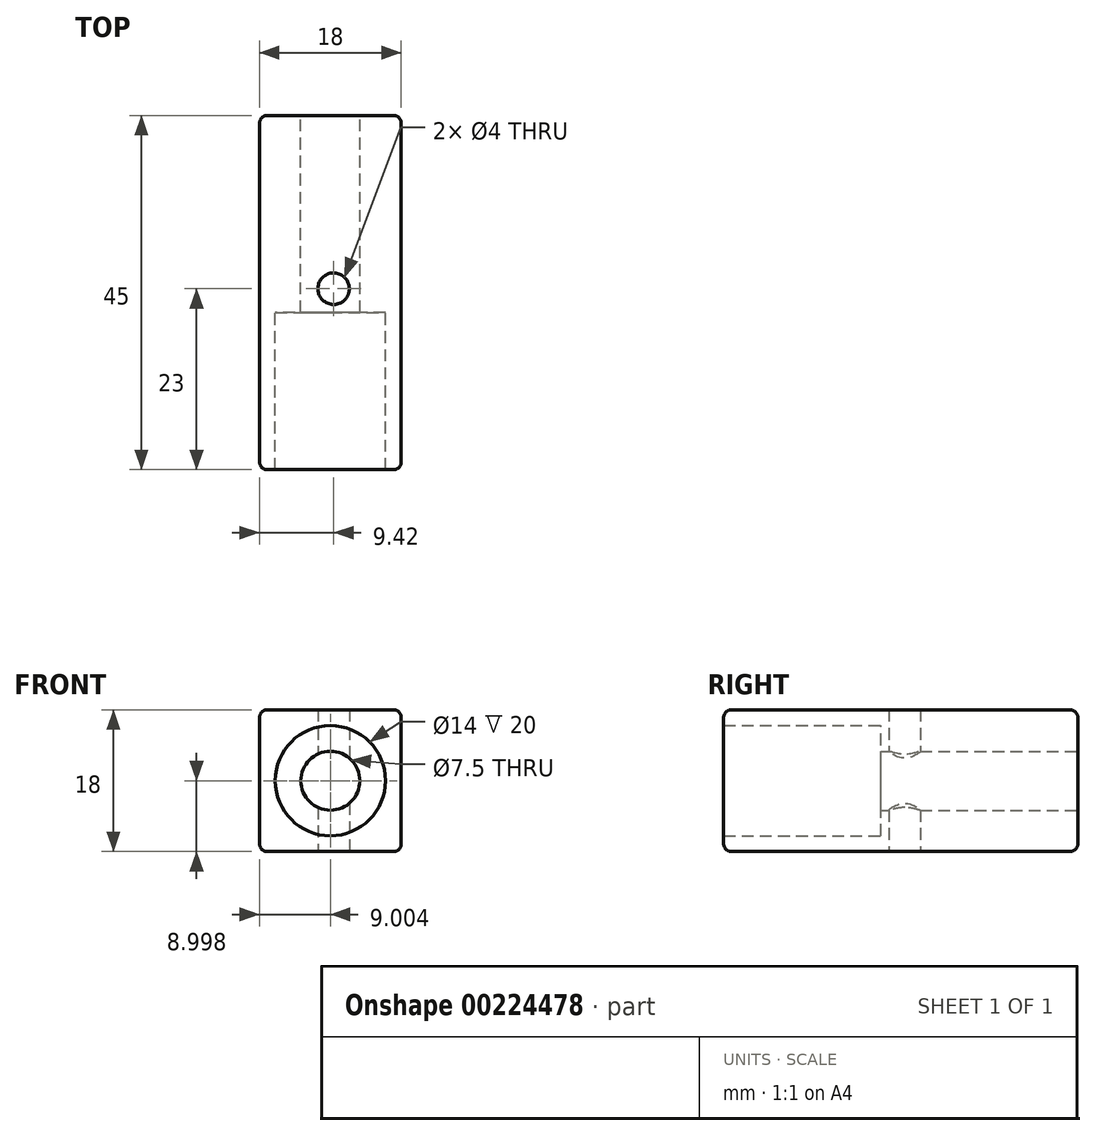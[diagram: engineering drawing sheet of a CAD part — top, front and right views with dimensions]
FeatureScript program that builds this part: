
annotation { "Feature Type Name" : "Feature", "Feature Type Description" : "" }
export const myFeature = defineFeature(function(context is Context, id is Id, definition is map)
    precondition{}
    {
        {
            var Q0;
            Q0=qCreatedBy(makeId("Front.planeOp"),FACE);
            var sketch = newSketch(context, id + "F0", { "sketchPlane" : qUnion([Q0])});
            skLineSegment(sketch, "E0.bottom", {"start": v(-9.42, 10.89) * mm, "end": v(8.58, 10.89) * mm});
            skLineSegment(sketch, "E0.top", {"start": v(-9.42, -7.11) * mm, "end": v(8.58, -7.11) * mm});
            skLineSegment(sketch, "E0.left", {"start": v(-9.42, 10.89) * mm, "end": v(-9.42, -7.11) * mm});
            skLineSegment(sketch, "E0.right", {"start": v(8.58, 10.89) * mm, "end": v(8.58, -7.11) * mm});
            skCircle(sketch, "E1", {"center": v(-0.42, 1.89) * mm, "radius": 7 * mm});
            skPoint(sketch, "E1.centerSnap0", {"position": v(-0.42, 10.89) * mm});
            skPoint(sketch, "E1.centerSnap1", {"position": v(8.58, 1.89) * mm});
            skCircle(sketch, "E2", {"center": v(-0.42, 1.89) * mm, "radius": 3.75 * mm});
            skSolve(sketch);
        }
        {
            var Q0;
            Q0=makeQuery(id+"F0.imprint","IMPRINT",FACE,{"disambiguationData":[TD([[makeQuery(id+"F0.imprint","IMPRINT",EDGE,{"derivedFrom":sQuery(id+"F0.wireOp",EDGE,"E0.bottom")}),-1.0]])]});
            extrude(context, id + "F1", {"entities" : qUnion([Q0]), "depth" : 45 * mm});
        }
        {
            var Q0;
            Q0=makeQuery(id+"F0.imprint","IMPRINT",FACE,{"disambiguationData":[TD([[makeQuery(id+"F0.imprint","IMPRINT",EDGE,{"derivedFrom":sQuery(id+"F0.wireOp",EDGE,"E1")}),1.0]])]});
            extrude(context, id + "F2", {"entities" : qUnion([Q0]), "operationType" : NewBodyOperationType.ADD, "depth" : 25 * mm});
        }
        {
            var Q0;
            Q0=makeQuery(id+"F1.opExtrude","SWEPT_FACE",FACE,{"disambiguationData":[OSD([sQuery(id+"F0.wireOp",EDGE,"E0.top")])]});
            var sketch = newSketch(context, id + "F3", { "sketchPlane" : qUnion([Q0])});
            skCircle(sketch, "E3", {"center": v(0, 22) * mm, "radius": 2 * mm});
            skSolve(sketch);
        }
        {
            var Q0;
            Q0=makeQuery(id+"F3.imprint","IMPRINT",FACE,{"disambiguationData":[TD([[makeQuery(id+"F3.imprint","IMPRINT",EDGE,{"derivedFrom":sQuery(id+"F3.wireOp",EDGE,"E3")}),1.0]])]});
            extrude(context, id + "F4", {"entities" : qUnion([Q0]), "operationType" : NewBodyOperationType.REMOVE, "oppositeDirection" : true, "depth" : 25 * mm});
        }
        {
            var Q0;
            Q0=makeQuery(id+"F1.opExtrude","SWEPT_EDGE",EDGE,{"disambiguationData":[OSD([sQuery(id+"F0.wireOp",EDGE,"E0.top"),sQuery(id+"F0.wireOp",EDGE,"E0.left")])]});
            var Q1;
            Q1=makeQuery(id+"F1.opExtrude","SWEPT_EDGE",EDGE,{"disambiguationData":[OSD([sQuery(id+"F0.wireOp",EDGE,"E0.top"),sQuery(id+"F0.wireOp",EDGE,"E0.right")])]});
            var Q2;
            Q2=makeQuery(id+"F1.opExtrude","SWEPT_EDGE",EDGE,{"disambiguationData":[OSD([sQuery(id+"F0.wireOp",EDGE,"E0.bottom"),sQuery(id+"F0.wireOp",EDGE,"E0.left")])]});
            var Q3;
            Q3=makeQuery(id+"F1.opExtrude","SWEPT_EDGE",EDGE,{"disambiguationData":[OSD([sQuery(id+"F0.wireOp",EDGE,"E0.bottom"),sQuery(id+"F0.wireOp",EDGE,"E0.right")])]});
            var Q4;
            Q4=makeQuery(id+"F1.opExtrude","CAP_EDGE",EDGE,{"disambiguationData":[OSD([sQuery(id+"F0.wireOp",EDGE,"E0.left")])],"isStart":true});
            var Q5;
            Q5=makeQuery(id+"F1.opExtrude","CAP_EDGE",EDGE,{"disambiguationData":[OSD([sQuery(id+"F0.wireOp",EDGE,"E0.bottom")])],"isStart":true});
            var Q6;
            Q6=makeQuery(id+"F1.opExtrude","CAP_EDGE",EDGE,{"disambiguationData":[OSD([sQuery(id+"F0.wireOp",EDGE,"E0.top")])],"isStart":true});
            var Q7;
            Q7=makeQuery(id+"F1.opExtrude","CAP_EDGE",EDGE,{"disambiguationData":[OSD([sQuery(id+"F0.wireOp",EDGE,"E0.right")])],"isStart":true});
            var Q8;
            Q8=makeQuery(id+"F1.opExtrude","CAP_EDGE",EDGE,{"disambiguationData":[OSD([sQuery(id+"F0.wireOp",EDGE,"E0.right")])],"isStart":false});
            var Q9;
            Q9=makeQuery(id+"F1.opExtrude","CAP_EDGE",EDGE,{"disambiguationData":[OSD([sQuery(id+"F0.wireOp",EDGE,"E0.bottom")])],"isStart":false});
            var Q10;
            Q10=makeQuery(id+"F1.opExtrude","CAP_EDGE",EDGE,{"disambiguationData":[OSD([sQuery(id+"F0.wireOp",EDGE,"E0.left")])],"isStart":false});
            var Q11;
            Q11=makeQuery(id+"F1.opExtrude","CAP_EDGE",EDGE,{"disambiguationData":[OSD([sQuery(id+"F0.wireOp",EDGE,"E0.top")])],"isStart":false});
            fillet(context, id + "F5", {"entities" : qUnion([Q0, Q1, Q2, Q3, Q4, Q5, Q6, Q7, Q8, Q9, Q10, Q11]), "radius" : 1 * mm, "tangentPropagation" : true, "allowEdgeOverflow" : false});
        }
    });
